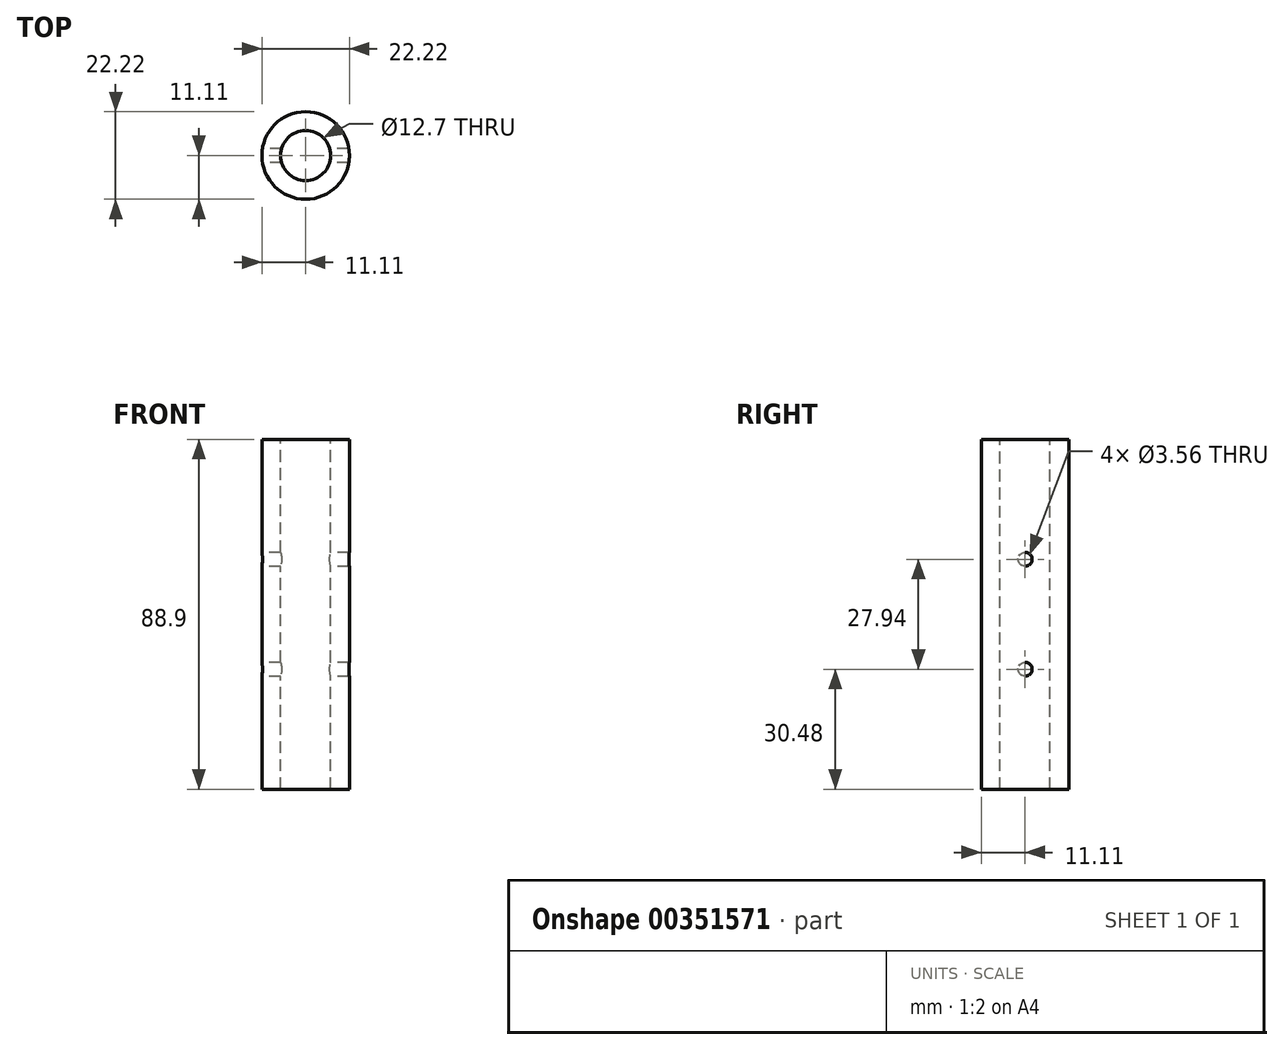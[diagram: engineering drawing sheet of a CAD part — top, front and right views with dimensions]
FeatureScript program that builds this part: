
annotation { "Feature Type Name" : "Feature", "Feature Type Description" : "" }
export const myFeature = defineFeature(function(context is Context, id is Id, definition is map)
    precondition{}
    {
        {
            var Q0;
            Q0=qCreatedBy(makeId("Top.planeOp"),FACE);
            var sketch = newSketch(context, id + "F0", { "sketchPlane" : qUnion([Q0])});
            skCircle(sketch, "E0", {"center": v(0, 0) * mm, "radius": 11.11 * mm});
            skSolve(sketch);
        }
        {
            var Q0;
            Q0 = qSketchRegion(id + "F0", true);
            extrude(context, id + "F1", {"entities" : qUnion([Q0]), "depth" : 88.9 * mm, "symmetric" : true});
        }
        {
            var Q0;
            Q0=makeQuery(id+"F1.opExtrude","CAP_FACE",FACE,{"disambiguationData":[OSD([sQuery(id+"F0.wireOp",EDGE,"E0")])],"isStart":false});
            var sketch = newSketch(context, id + "F2", { "sketchPlane" : qUnion([Q0])});
            skCircle(sketch, "E1", {"center": v(0, 0) * mm, "radius": 6.35 * mm});
            skSolve(sketch);
        }
        {
            var Q0;
            Q0 = qSketchRegion(id + "F2", true);
            var Q1;
            Q1=makeQuery(id+"F1.opExtrude","CAP_FACE",FACE,{"disambiguationData":[OSD([sQuery(id+"F0.wireOp",EDGE,"E0")])],"isStart":true});
            extrude(context, id + "F3", {"entities" : qUnion([Q0]), "operationType" : NewBodyOperationType.REMOVE, "endBound" : BoundingType.UP_TO_SURFACE, "oppositeDirection" : true, "endBoundEntityFace" : qUnion([Q1]), "depth" : 25.4 * mm});
        }
        {
            var Q0;
            Q0=qCreatedBy(makeId("Right.planeOp"),FACE);
            var sketch = newSketch(context, id + "F4", { "sketchPlane" : qUnion([Q0])});
            skCircle(sketch, "E2", {"center": v(0, -13.97) * mm, "radius": 1.78 * mm});
            skCircle(sketch, "E3.MirrorC", {"center": v(0, 13.97) * mm, "radius": 1.78 * mm});
            skSolve(sketch);
        }
        {
            var Q0;
            Q0 = qSketchRegion(id + "F4", true);
            extrude(context, id + "F5", {"entities" : qUnion([Q0]), "operationType" : NewBodyOperationType.REMOVE, "endBound" : BoundingType.THROUGH_ALL, "depth" : 25.4 * mm, "hasSecondDirection" : true, "secondDirectionBound" : BoundingType.THROUGH_ALL, "secondDirectionOppositeDirection" : true, "secondDirectionDepth" : 25.4 * mm});
        }
    });
